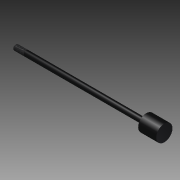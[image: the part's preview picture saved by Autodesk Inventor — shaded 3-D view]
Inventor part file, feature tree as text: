
AUTODESK INVENTOR PART (.ipt)
format: ipt  version: 2011 SP1 (Build 150282100, 282)  size: 119,808 bytes
history: native  units: in
note: dims shown in document units (in); Inventor stores cm internally (conversion verified against a paired STEP export)
features: other x70, revolve x3, sketch x3, thread x1
ambient origin geometry x8: Origin, YZ Plane, XZ Plane, XY Plane, X Axis, Y Axis, Z Axis, Center Point
bodies: Solid1 (feature_tree)
feature tree (77):
  revolve  "Revolution1"  Angle=360.0deg
  revolve  "Revolution2"  Angle=360.0deg
  thread  "Thread1"  [1 undecoded]
  revolve  "Revolution3"  [1 undecoded]
  other  "dia1_XY"
  other  "dia1_YZ"
  other  "dia1_ZX"
  other  "dia1_X"
  other  "dia1_Y"
  other  "dia1_Z"
  other  "dia1_Center"
  other  "dia12_XY"
  other  "dia12_YZ"
  other  "dia12_ZX"
  other  "dia12_X"
  other  "dia12_Y"
  other  "dia12_Z"
  other  "dia12_Center"
  other  "dia2_XY"
  other  "dia2_YZ"
  other  "dia2_ZX"
  other  "dia2_X"
  other  "dia2_Y"
  other  "dia2_Z"
  other  "dia2_Center"
  other  "dia22_XY"
  other  "dia22_YZ"
  other  "dia22_ZX"
  other  "dia22_X"
  other  "dia22_Y"
  other  "dia22_Z"
  other  "dia22_Center"
  other  "rl1_XY"
  other  "rl1_YZ"
  other  "rl1_ZX"
  other  "rl1_X"
  other  "rl1_Y"
  other  "rl1_Z"
  other  "rl1_Center"
  other  "rl2_XY"
  other  "rl2_YZ"
  other  "rl2_ZX"
  other  "rl2_X"
  other  "rl2_Y"
  other  "rl2_Z"
  other  "rl2_Center"
  other  "rod_cp_XY"
  other  "rod_cp_YZ"
  other  "rod_cp_ZX"
  other  "rod_cp_X"
  other  "rod_cp_Y"
  other  "rod_cp_Z"
  other  "rod_cp_Center"
  other  "thd1_XY"
  other  "thd1_YZ"
  other  "thd1_ZX"
  other  "thd1_X"
  other  "thd1_Y"
  other  "thd1_Z"
  other  "thd1_Center"
  other  "thd2_XY"
  other  "thd2_YZ"
  other  "thd2_ZX"
  other  "thd2_X"
  other  "thd2_Y"
  other  "thd2_Z"
  other  "thd2_Center"
  other  "to_rod_clevis_XY"
  other  "to_rod_clevis_YZ"
  other  "to_rod_clevis_ZX"
  other  "to_rod_clevis_X"
  other  "to_rod_clevis_Y"
  other  "to_rod_clevis_Z"
  other  "to_rod_clevis_Center"
  sketch  "Sketch_1"  dims[d0=360.0deg d1=360.0deg]
  sketch  "Sketch_3"  dims[d2=0.4787in d3=0.0in d4=360.0deg d5=0.0in d6=0.0in d7=0.0in]
  sketch  "Sketch_30"
note: 2 required parameter values undecoded (feature->parameter linkage not recoverable at this tier; creation-order binding heuristic only, values carry confidence <= 0.55)
